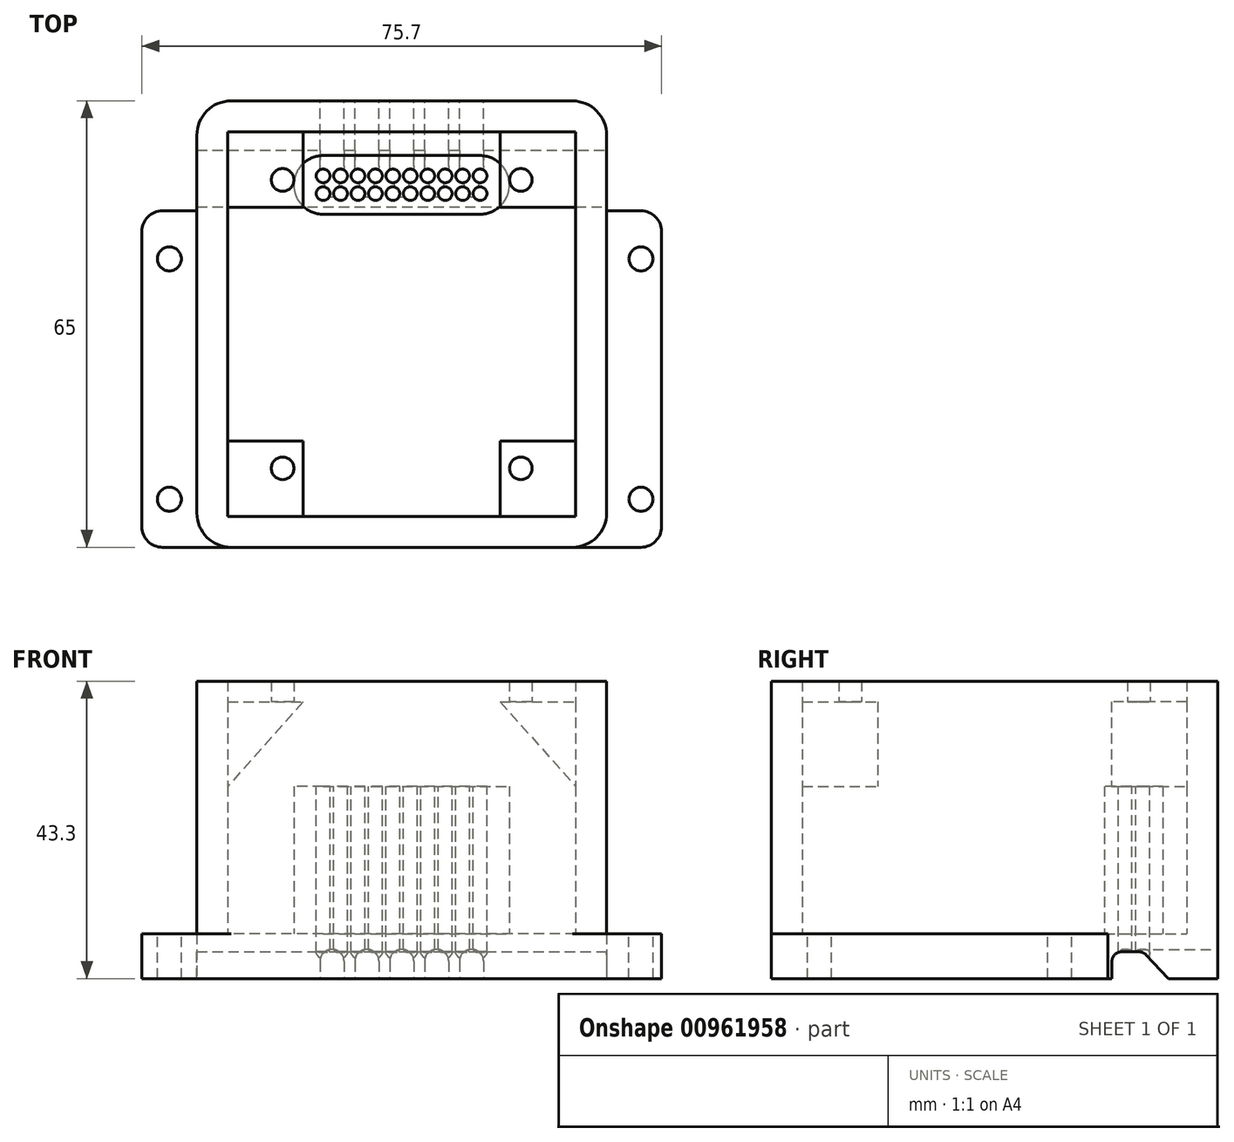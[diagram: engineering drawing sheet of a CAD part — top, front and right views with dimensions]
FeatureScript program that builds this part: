
annotation { "Feature Type Name" : "Feature", "Feature Type Description" : "" }
export const myFeature = defineFeature(function(context is Context, id is Id, definition is map)
    precondition{}
    {
        {
            var Q0;
            Q0=qCreatedBy(makeId("Top.planeOp"),FACE);
            var sketch = newSketch(context, id + "F0", { "sketchPlane" : qUnion([Q0])});
            skLineSegment(sketch, "E0.bottom", {"start": v(22.35, -25) * mm, "end": v(-22.35, -25) * mm});
            skLineSegment(sketch, "E0.top", {"start": v(22.35, 25) * mm, "end": v(-22.35, 25) * mm});
            skLineSegment(sketch, "E0.left", {"start": v(22.35, -25) * mm, "end": v(22.35, 25) * mm});
            skLineSegment(sketch, "E0.right", {"start": v(-22.35, -25) * mm, "end": v(-22.35, 25) * mm});
            skPoint(sketch, "E0.middle", {"position": v(0, 0) * mm});
            skSolve(sketch);
        }
        {
            var Q0;
            Q0=qCreatedBy(makeId("Top.planeOp"),FACE);
            var sketch = newSketch(context, id + "F1", { "sketchPlane" : qUnion([Q0])});
            skLineSegment(sketch, "E1.bottom", {"start": v(29.85, -32.5) * mm, "end": v(-29.85, -32.5) * mm});
            skLineSegment(sketch, "E1.top", {"start": v(24.85, 32.5) * mm, "end": v(-24.85, 32.5) * mm});
            skLineSegment(sketch, "E1.left", {"start": v(29.85, -32.5) * mm, "end": v(29.85, 27.5) * mm});
            skLineSegment(sketch, "E1.right", {"start": v(-29.85, -32.5) * mm, "end": v(-29.85, 27.5) * mm});
            skPoint(sketch, "E1.middle", {"position": v(0, 0) * mm});
            skPoint(sketch, "E2.visualSharp", {"position": v(-29.85, 32.5) * mm});
            skArc(sketch, "E2.filletArc", {"start": v(-24.85, 32.5) * mm, "mid": v(-28.39, 31.04) * mm, "end": v(-29.85, 27.5) * mm});
            skPoint(sketch, "E3.visualSharp", {"position": v(29.85, 32.5) * mm});
            skArc(sketch, "E3.filletArc", {"start": v(29.85, 27.5) * mm, "mid": v(28.39, 31.04) * mm, "end": v(24.85, 32.5) * mm});
            skPoint(sketch, "E4.visualSharp", {"position": v(-29.85, -32.5) * mm});
            skPoint(sketch, "E5.visualSharp", {"position": v(29.85, -32.5) * mm});
            skLineSegment(sketch, "E6", {"start": v(-20.98, 18.5) * mm, "end": v(20.45, 18.5) * mm, "construction": true});
            skLineSegment(sketch, "E7.bottom", {"start": v(-29.85, -32.5) * mm, "end": v(-34.85, -32.5) * mm});
            skLineSegment(sketch, "E7.top", {"start": v(-29.85, 16.5) * mm, "end": v(-34.85, 16.5) * mm});
            skLineSegment(sketch, "E7.left", {"start": v(-29.85, -32.5) * mm, "end": v(-29.85, 16.5) * mm});
            skLineSegment(sketch, "E7.right", {"start": v(-37.85, -29.5) * mm, "end": v(-37.85, 13.5) * mm});
            skPoint(sketch, "E8.oppositeSnap0", {"position": v(-33.85, 16.5) * mm});
            skLineSegment(sketch, "E8.bottom", {"start": v(29.85, -32.5) * mm, "end": v(34.85, -32.5) * mm});
            skLineSegment(sketch, "E8.top", {"start": v(29.85, 16.5) * mm, "end": v(34.85, 16.5) * mm});
            skLineSegment(sketch, "E8.left", {"start": v(29.85, -32.5) * mm, "end": v(29.85, 16.5) * mm});
            skLineSegment(sketch, "E8.right", {"start": v(37.85, -29.5) * mm, "end": v(37.85, 13.5) * mm});
            skPoint(sketch, "E9.visualSharp", {"position": v(-37.85, 16.5) * mm});
            skArc(sketch, "E9.filletArc", {"start": v(-34.85, 16.5) * mm, "mid": v(-36.97, 15.62) * mm, "end": v(-37.85, 13.5) * mm});
            skPoint(sketch, "E10.visualSharp", {"position": v(-37.85, -32.5) * mm});
            skArc(sketch, "E10.filletArc", {"start": v(-37.85, -29.5) * mm, "mid": v(-36.97, -31.62) * mm, "end": v(-34.85, -32.5) * mm});
            skPoint(sketch, "E11.visualSharp", {"position": v(37.85, 16.5) * mm});
            skArc(sketch, "E11.filletArc", {"start": v(37.85, 13.5) * mm, "mid": v(36.97, 15.62) * mm, "end": v(34.85, 16.5) * mm});
            skPoint(sketch, "E12.visualSharp", {"position": v(37.85, -32.5) * mm});
            skArc(sketch, "E12.filletArc", {"start": v(34.85, -32.5) * mm, "mid": v(36.97, -31.62) * mm, "end": v(37.85, -29.5) * mm});
            skSolve(sketch);
        }
        {
            var Q0;
            Q0=makeQuery(id+"F1.imprint","IMPRINT",FACE,{"disambiguationData":[TD([[makeQuery(id+"F1.imprint","IMPRINT",EDGE,{"derivedFrom":sQuery(id+"F1.wireOp",EDGE,"E1.bottom")}),-1.0]])]});
            var Q1;
            Q1=makeQuery(id+"F1.imprint","IMPRINT",FACE,{"disambiguationData":[TD([[makeQuery(id+"F1.imprint","IMPRINT",EDGE,{"derivedFrom":sQuery(id+"F1.wireOp",EDGE,"E7.bottom")}),-1.0]])]});
            var Q2;
            Q2=makeQuery(id+"F1.imprint","IMPRINT",FACE,{"disambiguationData":[TD([[makeQuery(id+"F1.imprint","IMPRINT",EDGE,{"derivedFrom":sQuery(id+"F1.wireOp",EDGE,"E8.bottom")}),1.0]])]});
            extrude(context, id + "F2", {"entities" : qUnion([Q0, Q1, Q2]), "depth" : 6.5 * mm, "offsetDistance" : 25 * mm});
        }
        {
            var Q0;
            Q0=makeQuery(id+"F2.opExtrude","CAP_FACE",FACE,{"disambiguationData":[OSD([sQuery(id+"F1.wireOp",EDGE,"E1.bottom"),sQuery(id+"F1.wireOp",EDGE,"E1.top"),sQuery(id+"F1.wireOp",EDGE,"E1.left"),sQuery(id+"F1.wireOp",EDGE,"E1.right"),sQuery(id+"F1.wireOp",EDGE,"E2.filletArc"),sQuery(id+"F1.wireOp",EDGE,"E3.filletArc"),sQuery(id+"F1.wireOp",EDGE,"E4.filletArc"),sQuery(id+"F1.wireOp",EDGE,"E5.filletArc")])],"isStart":false});
            var sketch = newSketch(context, id + "F3", { "sketchPlane" : qUnion([Q0])});
            skLineSegment(sketch, "E13.bottom", {"start": v(25.35, -28) * mm, "end": v(-25.35, -28) * mm});
            skLineSegment(sketch, "E13.top", {"start": v(25.35, 28) * mm, "end": v(-25.35, 28) * mm});
            skLineSegment(sketch, "E13.left", {"start": v(25.35, -28) * mm, "end": v(25.35, 28) * mm});
            skLineSegment(sketch, "E13.right", {"start": v(-25.35, -28) * mm, "end": v(-25.35, 28) * mm});
            skPoint(sketch, "E13.middle", {"position": v(0, 0) * mm});
            skLineSegment(sketch, "E14.bottom", {"start": v(-15.24, 28) * mm, "end": v(15.24, 28) * mm});
            skLineSegment(sketch, "E14.top", {"start": v(-11.45, 16) * mm, "end": v(11.4, 16) * mm});
            skPoint(sketch, "E15", {"position": v(-11.45, 19) * mm});
            skPoint(sketch, "E16", {"position": v(-8.91, 19) * mm});
            skPoint(sketch, "E17", {"position": v(-6.37, 19) * mm});
            skPoint(sketch, "E18", {"position": v(-3.83, 19) * mm});
            skPoint(sketch, "E19", {"position": v(-1.3, 19) * mm});
            skPoint(sketch, "E20", {"position": v(1.25, 19) * mm});
            skPoint(sketch, "E21", {"position": v(3.79, 19) * mm});
            skPoint(sketch, "E22", {"position": v(6.33, 19) * mm});
            skPoint(sketch, "E23", {"position": v(8.87, 19) * mm});
            skPoint(sketch, "E24", {"position": v(11.4, 19) * mm});
            skPoint(sketch, "E25.visualSharp", {"position": v(15.24, 16) * mm});
            skLineSegment(sketch, "E26.top", {"start": v(-11.45, 24.54) * mm, "end": v(11.4, 24.54) * mm});
            skArc(sketch, "E27", {"start": v(-11.45, 24.54) * mm, "mid": v(-15.72, 20.27) * mm, "end": v(-11.45, 16) * mm});
            skArc(sketch, "E28", {"start": v(11.4, 16) * mm, "mid": v(15.68, 20.27) * mm, "end": v(11.4, 24.54) * mm});
            skLineSegment(sketch, "E29.bottom", {"start": v(24.85, -32.5) * mm, "end": v(-24.85, -32.5) * mm});
            skLineSegment(sketch, "E29.top", {"start": v(24.85, 32.5) * mm, "end": v(-24.85, 32.5) * mm});
            skLineSegment(sketch, "E29.left", {"start": v(29.85, -27.5) * mm, "end": v(29.85, 27.5) * mm});
            skLineSegment(sketch, "E29.right", {"start": v(-29.85, -27.5) * mm, "end": v(-29.85, 27.5) * mm});
            skPoint(sketch, "E30.visualSharp", {"position": v(-29.85, -32.5) * mm});
            skArc(sketch, "E30.filletArc", {"start": v(-29.85, -27.5) * mm, "mid": v(-28.39, -31.04) * mm, "end": v(-24.85, -32.5) * mm});
            skPoint(sketch, "E31.visualSharp", {"position": v(29.85, -32.5) * mm});
            skArc(sketch, "E31.filletArc", {"start": v(24.85, -32.5) * mm, "mid": v(28.39, -31.04) * mm, "end": v(29.85, -27.5) * mm});
            skPoint(sketch, "E32.visualSharp", {"position": v(-29.85, 32.5) * mm});
            skArc(sketch, "E32.filletArc", {"start": v(-24.85, 32.5) * mm, "mid": v(-28.39, 31.04) * mm, "end": v(-29.85, 27.5) * mm});
            skPoint(sketch, "E33.visualSharp", {"position": v(29.85, 32.5) * mm});
            skArc(sketch, "E33.filletArc", {"start": v(29.85, 27.5) * mm, "mid": v(28.39, 31.04) * mm, "end": v(24.85, 32.5) * mm});
            skPoint(sketch, "E34", {"position": v(-6.37, 21.54) * mm});
            skPoint(sketch, "E35", {"position": v(-11.45, 21.54) * mm});
            skPoint(sketch, "E36", {"position": v(-8.91, 21.54) * mm});
            skPoint(sketch, "E37", {"position": v(-3.83, 21.54) * mm});
            skPoint(sketch, "E38", {"position": v(-1.3, 21.54) * mm});
            skPoint(sketch, "E39", {"position": v(1.25, 21.54) * mm});
            skPoint(sketch, "E40", {"position": v(3.79, 21.54) * mm});
            skPoint(sketch, "E41", {"position": v(6.33, 21.54) * mm});
            skPoint(sketch, "E42", {"position": v(8.87, 21.54) * mm});
            skPoint(sketch, "E43", {"position": v(11.4, 21.54) * mm});
            skSolve(sketch);
        }
        {
            var Q0;
            Q0=makeQuery(id+"F3.imprint","IMPRINT",FACE,{"disambiguationData":[TD([[makeQuery(id+"F3.imprint","IMPRINT",EDGE,{"derivedFrom":sQuery(id+"F3.wireOp",EDGE,"E13.bottom")}),1.0]])]});
            var Q1;
            Q1=makeQuery(id+"F3.imprint","IMPRINT",FACE,{"disambiguationData":[TD([[makeQuery(id+"F3.imprint","IMPRINT",EDGE,{"derivedFrom":sQuery(id+"F3.wireOp",EDGE,"E14.top")}),1.0]])]});
            extrude(context, id + "F4", {"entities" : qUnion([Q0, Q1]), "operationType" : NewBodyOperationType.ADD, "depth" : 21.5 * mm, "offsetDistance" : 25 * mm});
        }
        {
            var Q0;
            {var subQ0=sQuery(id+"F1.wireOp",EDGE,"E1.left");Q0=makeQuery(id+"F4.boolean.opBoolean","MERGE",FACE,{"derivedFrom":[makeQuery(id+"F2.opExtrude","SWEPT_FACE",FACE,{"disambiguationData":[OSD([subQ0])]}),makeQuery(id+"F4.opExtrude","SWEPT_FACE",FACE,{"disambiguationData":[OSD([subQ0])]})]});}
            var sketch = newSketch(context, id + "F5", { "sketchPlane" : qUnion([Q0])});
            skLineSegment(sketch, "E44", {"start": v(18.5, 18.6) * mm, "end": v(18.5, -3.34) * mm, "construction": true});
            skPoint(sketch, "E45", {"position": v(18.5, 2.5) * mm});
            skCircle(sketch, "E46", {"center": v(18.5, 2.5) * mm, "radius": 1.4 * mm});
            skLineSegment(sketch, "E47", {"start": v(17.1, 2.5) * mm, "end": v(17.1, 0) * mm});
            skCircle(sketch, "E48", {"center": v(21.04, 2.5) * mm, "radius": 1.4 * mm});
            skLineSegment(sketch, "E49", {"start": v(-11765.86, 3.9) * mm, "end": v(18.5, 3.9) * mm});
            skLineSegment(sketch, "E50", {"start": v(22.06, 3.46) * mm, "end": v(25.34, 0) * mm});
            skLineSegment(sketch, "E51", {"start": v(18.5, 3.9) * mm, "end": v(21.04, 3.9) * mm});
            skSolve(sketch);
        }
        {
            var Q0;
            {var subQ0=sQuery(id+"F5.wireOp",EDGE,"E46");var subQ1=makeQuery(id+"F5.imprint","INTERSECT",VERTEX,{"derivedFrom":[subQ0,sQuery(id+"F5.wireOp",EDGE,"E47")]});Q0=makeQuery(id+"F5.imprint","IMPRINT",FACE,{"disambiguationData":[TD([[makeQuery(id+"F5.imprint","IMPRINT",EDGE,{"disambiguationData":[TD([[subQ1,1.0]])],"derivedFrom":subQ0}),1.0]])]});}
            var Q1;
            {var subQ0=sQuery(id+"F5.wireOp",EDGE,"E47");Q1=makeQuery(id+"F5.imprint","IMPRINT",FACE,{"disambiguationData":[TD([[makeQuery(id+"F5.imprint","IMPRINT",EDGE,{"derivedFrom":subQ0}),1.0]])]});}
            var Q2;
            {var subQ0=sQuery(id+"F5.wireOp",EDGE,"E51");Q2=makeQuery(id+"F5.imprint","IMPRINT",FACE,{"disambiguationData":[TD([[makeQuery(id+"F5.imprint","IMPRINT",EDGE,{"derivedFrom":subQ0}),-1.0]])]});}
            var Q3;
            {var subQ0=sQuery(id+"F5.wireOp",EDGE,"E48");var subQ1=sQuery(id+"F5.wireOp",EDGE,"E46");var subQ2=makeQuery(id+"F5.imprint","INTERSECT",VERTEX,{"disambiguationData":[OD(0.0)],"derivedFrom":[subQ1,subQ0]});Q3=makeQuery(id+"F5.imprint","IMPRINT",FACE,{"disambiguationData":[TD([[makeQuery(id+"F5.imprint","IMPRINT",EDGE,{"disambiguationData":[TD([[subQ2,1.0]])],"derivedFrom":subQ1}),-1.0]])]});}
            var Q4;
            {var subQ0=sQuery(id+"F5.wireOp",EDGE,"E48");var subQ1=sQuery(id+"F5.wireOp",EDGE,"E46");var subQ2=makeQuery(id+"F5.imprint","INTERSECT",VERTEX,{"disambiguationData":[OD(0.0)],"derivedFrom":[subQ1,subQ0]});Q4=makeQuery(id+"F5.imprint","IMPRINT",FACE,{"disambiguationData":[TD([[makeQuery(id+"F5.imprint","IMPRINT",EDGE,{"disambiguationData":[TD([[subQ2,1.0]])],"derivedFrom":subQ1}),1.0]])]});}
            extrude(context, id + "F6", {"entities" : qUnion([Q0, Q1, Q2, Q3, Q4]), "operationType" : NewBodyOperationType.REMOVE, "endBound" : BoundingType.THROUGH_ALL, "oppositeDirection" : true, "depth" : 25 * mm, "offsetDistance" : 25 * mm});
        }
        {
            var Q0;
            Q0=makeQuery(id+"F4.opExtrude","CAP_FACE",FACE,{"disambiguationData":[OSD([sQuery(id+"F3.wireOp",EDGE,"E13.bottom"),sQuery(id+"F3.wireOp",EDGE,"E13.top"),sQuery(id+"F3.wireOp",EDGE,"E13.left"),sQuery(id+"F3.wireOp",EDGE,"E13.right"),sQuery(id+"F3.wireOp",EDGE,"E29.bottom"),sQuery(id+"F3.wireOp",EDGE,"E29.top"),sQuery(id+"F3.wireOp",EDGE,"E29.left"),sQuery(id+"F3.wireOp",EDGE,"E29.right"),sQuery(id+"F3.wireOp",EDGE,"E30.filletArc"),sQuery(id+"F3.wireOp",EDGE,"E31.filletArc"),sQuery(id+"F3.wireOp",EDGE,"E32.filletArc"),sQuery(id+"F3.wireOp",EDGE,"E33.filletArc")])],"isStart":false});
            var sketch = newSketch(context, id + "F7", { "sketchPlane" : qUnion([Q0])});
            skPoint(sketch, "E52", {"position": v(-11.45, 19) * mm});
            skCircle(sketch, "E53", {"center": v(-11.45, 19) * mm, "radius": 1 * mm});
            skPoint(sketch, "E54", {"position": v(-8.91, 19) * mm});
            skPoint(sketch, "E55", {"position": v(-6.37, 19) * mm});
            skPoint(sketch, "E56", {"position": v(-3.83, 19) * mm});
            skPoint(sketch, "E57", {"position": v(-1.3, 19) * mm});
            skPoint(sketch, "E58", {"position": v(1.25, 19) * mm});
            skPoint(sketch, "E59", {"position": v(3.79, 19) * mm});
            skPoint(sketch, "E60", {"position": v(6.33, 19) * mm});
            skPoint(sketch, "E61", {"position": v(8.87, 19) * mm});
            skPoint(sketch, "E62", {"position": v(11.4, 19) * mm});
            skCircle(sketch, "E63", {"center": v(-8.91, 19) * mm, "radius": 1 * mm});
            skCircle(sketch, "E64", {"center": v(-6.37, 19) * mm, "radius": 1 * mm});
            skCircle(sketch, "E65", {"center": v(-3.83, 19) * mm, "radius": 1 * mm});
            skCircle(sketch, "E66", {"center": v(-1.3, 19) * mm, "radius": 1 * mm});
            skCircle(sketch, "E67", {"center": v(1.25, 19) * mm, "radius": 1 * mm});
            skCircle(sketch, "E68", {"center": v(3.79, 19) * mm, "radius": 1 * mm});
            skCircle(sketch, "E69", {"center": v(6.33, 19) * mm, "radius": 1 * mm});
            skCircle(sketch, "E70", {"center": v(8.87, 19) * mm, "radius": 1 * mm});
            skCircle(sketch, "E71", {"center": v(11.4, 19) * mm, "radius": 1 * mm});
            skPoint(sketch, "E72", {"position": v(-11.45, 21.58) * mm});
            skPoint(sketch, "E73", {"position": v(-8.91, 21.58) * mm});
            skPoint(sketch, "E74", {"position": v(-6.37, 21.58) * mm});
            skPoint(sketch, "E75", {"position": v(-3.83, 21.58) * mm});
            skPoint(sketch, "E76", {"position": v(-1.3, 21.58) * mm});
            skPoint(sketch, "E77", {"position": v(1.25, 21.58) * mm});
            skPoint(sketch, "E78", {"position": v(3.79, 21.58) * mm});
            skPoint(sketch, "E79", {"position": v(6.33, 21.58) * mm});
            skPoint(sketch, "E80", {"position": v(8.87, 21.58) * mm});
            skPoint(sketch, "E81", {"position": v(11.4, 21.58) * mm});
            skCircle(sketch, "E82", {"center": v(-11.45, 21.58) * mm, "radius": 1 * mm});
            skCircle(sketch, "E83", {"center": v(-8.91, 21.58) * mm, "radius": 1 * mm});
            skCircle(sketch, "E84", {"center": v(-6.37, 21.58) * mm, "radius": 1 * mm});
            skCircle(sketch, "E85", {"center": v(-3.83, 21.58) * mm, "radius": 1 * mm});
            skCircle(sketch, "E86", {"center": v(-4.8, 18.76) * mm, "radius": 0.8 * mm});
            skCircle(sketch, "E87", {"center": v(-1.3, 21.58) * mm, "radius": 1 * mm});
            skCircle(sketch, "E88", {"center": v(1.25, 21.58) * mm, "radius": 1 * mm});
            skCircle(sketch, "E89", {"center": v(3.79, 21.58) * mm, "radius": 1 * mm});
            skCircle(sketch, "E90", {"center": v(6.33, 21.58) * mm, "radius": 1 * mm});
            skCircle(sketch, "E91", {"center": v(8.87, 21.58) * mm, "radius": 1 * mm});
            skCircle(sketch, "E92", {"center": v(11.4, 21.58) * mm, "radius": 1 * mm});
            skSolve(sketch);
        }
        {
            var Q0;
            {var subQ0=sQuery(id+"F1.wireOp",EDGE,"E1.left");Q0=makeQuery(id+"F4.boolean.opBoolean","MERGE",FACE,{"derivedFrom":[makeQuery(id+"F2.opExtrude","SWEPT_FACE",FACE,{"disambiguationData":[OSD([subQ0])]}),makeQuery(id+"F4.opExtrude","SWEPT_FACE",FACE,{"disambiguationData":[OSD([subQ0])]})]});}
            var sketch = newSketch(context, id + "F8", { "sketchPlane" : qUnion([Q0])});
            skSolve(sketch);
        }
        {
            var Q0;
            Q0=makeQuery(id+"F7.imprint","IMPRINT",FACE,{"disambiguationData":[TD([[makeQuery(id+"F7.imprint","IMPRINT",EDGE,{"derivedFrom":sQuery(id+"F7.wireOp",EDGE,"E66")}),1.0]])]});
            var Q1;
            Q1=makeQuery(id+"F7.imprint","IMPRINT",FACE,{"disambiguationData":[TD([[makeQuery(id+"F7.imprint","IMPRINT",EDGE,{"derivedFrom":sQuery(id+"F7.wireOp",EDGE,"E53")}),1.0]])]});
            var Q2;
            Q2=makeQuery(id+"F7.imprint","IMPRINT",FACE,{"disambiguationData":[TD([[makeQuery(id+"F7.imprint","IMPRINT",EDGE,{"derivedFrom":sQuery(id+"F7.wireOp",EDGE,"E63")}),1.0]])]});
            var Q3;
            Q3=makeQuery(id+"F7.imprint","IMPRINT",FACE,{"disambiguationData":[TD([[makeQuery(id+"F7.imprint","IMPRINT",EDGE,{"derivedFrom":sQuery(id+"F7.wireOp",EDGE,"E64")}),1.0]])]});
            var Q4;
            Q4=makeQuery(id+"F7.imprint","IMPRINT",FACE,{"disambiguationData":[TD([[makeQuery(id+"F7.imprint","IMPRINT",EDGE,{"derivedFrom":sQuery(id+"F7.wireOp",EDGE,"E65")}),1.0]])]});
            var Q5;
            Q5=makeQuery(id+"F7.imprint","IMPRINT",FACE,{"disambiguationData":[TD([[makeQuery(id+"F7.imprint","IMPRINT",EDGE,{"derivedFrom":sQuery(id+"F7.wireOp",EDGE,"E67")}),1.0]])]});
            var Q6;
            Q6=makeQuery(id+"F7.imprint","IMPRINT",FACE,{"disambiguationData":[TD([[makeQuery(id+"F7.imprint","IMPRINT",EDGE,{"derivedFrom":sQuery(id+"F7.wireOp",EDGE,"E68")}),1.0]])]});
            var Q7;
            Q7=makeQuery(id+"F7.imprint","IMPRINT",FACE,{"disambiguationData":[TD([[makeQuery(id+"F7.imprint","IMPRINT",EDGE,{"derivedFrom":sQuery(id+"F7.wireOp",EDGE,"E69")}),1.0]])]});
            var Q8;
            Q8=makeQuery(id+"F7.imprint","IMPRINT",FACE,{"disambiguationData":[TD([[makeQuery(id+"F7.imprint","IMPRINT",EDGE,{"derivedFrom":sQuery(id+"F7.wireOp",EDGE,"E70")}),1.0]])]});
            var Q9;
            Q9=makeQuery(id+"F7.imprint","IMPRINT",FACE,{"disambiguationData":[TD([[makeQuery(id+"F7.imprint","IMPRINT",EDGE,{"derivedFrom":sQuery(id+"F7.wireOp",EDGE,"E71")}),1.0]])]});
            var Q10;
            Q10=makeQuery(id+"F7.imprint","IMPRINT",FACE,{"disambiguationData":[TD([[makeQuery(id+"F7.imprint","IMPRINT",EDGE,{"derivedFrom":sQuery(id+"F7.wireOp",EDGE,"E82")}),1.0]])]});
            var Q11;
            Q11=makeQuery(id+"F7.imprint","IMPRINT",FACE,{"disambiguationData":[TD([[makeQuery(id+"F7.imprint","IMPRINT",EDGE,{"derivedFrom":sQuery(id+"F7.wireOp",EDGE,"E83")}),1.0]])]});
            var Q12;
            Q12=makeQuery(id+"F7.imprint","IMPRINT",FACE,{"disambiguationData":[TD([[makeQuery(id+"F7.imprint","IMPRINT",EDGE,{"derivedFrom":sQuery(id+"F7.wireOp",EDGE,"E84")}),1.0]])]});
            var Q13;
            Q13=makeQuery(id+"F7.imprint","IMPRINT",FACE,{"disambiguationData":[TD([[makeQuery(id+"F7.imprint","IMPRINT",EDGE,{"derivedFrom":sQuery(id+"F7.wireOp",EDGE,"E85")}),1.0]])]});
            var Q14;
            Q14=makeQuery(id+"F7.imprint","IMPRINT",FACE,{"disambiguationData":[TD([[makeQuery(id+"F7.imprint","IMPRINT",EDGE,{"derivedFrom":sQuery(id+"F7.wireOp",EDGE,"E87")}),1.0]])]});
            var Q15;
            Q15=makeQuery(id+"F7.imprint","IMPRINT",FACE,{"disambiguationData":[TD([[makeQuery(id+"F7.imprint","IMPRINT",EDGE,{"derivedFrom":sQuery(id+"F7.wireOp",EDGE,"E88")}),1.0]])]});
            var Q16;
            Q16=makeQuery(id+"F7.imprint","IMPRINT",FACE,{"disambiguationData":[TD([[makeQuery(id+"F7.imprint","IMPRINT",EDGE,{"derivedFrom":sQuery(id+"F7.wireOp",EDGE,"E89")}),1.0]])]});
            var Q17;
            Q17=makeQuery(id+"F7.imprint","IMPRINT",FACE,{"disambiguationData":[TD([[makeQuery(id+"F7.imprint","IMPRINT",EDGE,{"derivedFrom":sQuery(id+"F7.wireOp",EDGE,"E90")}),1.0]])]});
            var Q18;
            Q18=makeQuery(id+"F7.imprint","IMPRINT",FACE,{"disambiguationData":[TD([[makeQuery(id+"F7.imprint","IMPRINT",EDGE,{"derivedFrom":sQuery(id+"F7.wireOp",EDGE,"E91")}),1.0]])]});
            var Q19;
            Q19=makeQuery(id+"F7.imprint","IMPRINT",FACE,{"disambiguationData":[TD([[makeQuery(id+"F7.imprint","IMPRINT",EDGE,{"derivedFrom":sQuery(id+"F7.wireOp",EDGE,"E92")}),1.0]])]});
            var Q20;
            Q20=qSketchRegion(id+"F8",true);
            extrude(context, id + "F9", {"entities" : qUnion([Q0, Q1, Q2, Q3, Q4, Q5, Q6, Q7, Q8, Q9, Q10, Q11, Q12, Q13, Q14, Q15, Q16, Q17, Q18, Q19, Q20]), "operationType" : NewBodyOperationType.REMOVE, "oppositeDirection" : true, "depth" : 26 * mm, "offsetDistance" : 25 * mm});
        }
        {
            var Q0;
            Q0=makeQuery(id+"F4.opExtrude","CAP_FACE",FACE,{"disambiguationData":[OSD([sQuery(id+"F3.wireOp",EDGE,"E13.bottom"),sQuery(id+"F3.wireOp",EDGE,"E13.top"),sQuery(id+"F3.wireOp",EDGE,"E13.left"),sQuery(id+"F3.wireOp",EDGE,"E13.right"),sQuery(id+"F3.wireOp",EDGE,"E29.bottom"),sQuery(id+"F3.wireOp",EDGE,"E29.top"),sQuery(id+"F3.wireOp",EDGE,"E29.left"),sQuery(id+"F3.wireOp",EDGE,"E29.right"),sQuery(id+"F3.wireOp",EDGE,"E30.filletArc"),sQuery(id+"F3.wireOp",EDGE,"E31.filletArc"),sQuery(id+"F3.wireOp",EDGE,"E32.filletArc"),sQuery(id+"F3.wireOp",EDGE,"E33.filletArc")])],"isStart":false});
            var sketch = newSketch(context, id + "F10", { "sketchPlane" : qUnion([Q0])});
            skLineSegment(sketch, "E93.bottom", {"start": v(-25.35, 28) * mm, "end": v(-14.35, 28) * mm});
            skLineSegment(sketch, "E93.top", {"start": v(-25.35, 17) * mm, "end": v(-14.35, 17) * mm});
            skLineSegment(sketch, "E93.left", {"start": v(-25.35, 28) * mm, "end": v(-25.35, 17) * mm});
            skLineSegment(sketch, "E93.right", {"start": v(-14.35, 28) * mm, "end": v(-14.35, 17) * mm});
            skLineSegment(sketch, "E94.bottom", {"start": v(25.35, 28) * mm, "end": v(14.35, 28) * mm});
            skLineSegment(sketch, "E94.top", {"start": v(25.35, 17) * mm, "end": v(14.35, 17) * mm});
            skLineSegment(sketch, "E94.left", {"start": v(25.35, 28) * mm, "end": v(25.35, 17) * mm});
            skLineSegment(sketch, "E94.right", {"start": v(14.35, 28) * mm, "end": v(14.35, 17) * mm});
            skLineSegment(sketch, "E95.bottom", {"start": v(-25.35, -28) * mm, "end": v(-14.35, -28) * mm});
            skLineSegment(sketch, "E95.top", {"start": v(-25.35, -17) * mm, "end": v(-14.35, -17) * mm});
            skLineSegment(sketch, "E95.left", {"start": v(-25.35, -28) * mm, "end": v(-25.35, -17) * mm});
            skLineSegment(sketch, "E95.right", {"start": v(-14.35, -28) * mm, "end": v(-14.35, -17) * mm});
            skLineSegment(sketch, "E96.bottom", {"start": v(25.35, -28) * mm, "end": v(14.35, -28) * mm});
            skLineSegment(sketch, "E96.top", {"start": v(25.35, -17) * mm, "end": v(14.35, -17) * mm});
            skLineSegment(sketch, "E96.left", {"start": v(25.35, -28) * mm, "end": v(25.35, -17) * mm});
            skLineSegment(sketch, "E96.right", {"start": v(14.35, -28) * mm, "end": v(14.35, -17) * mm});
            skSolve(sketch);
        }
        {
            var Q0;
            {var subQ5=sQuery(id+"F10.wireOp",EDGE,"E93.bottom");Q0=makeQuery(id+"F10.imprint","IMPRINT",FACE,{"disambiguationData":[TD([[makeQuery(id+"F10.imprint","IMPRINT",EDGE,{"derivedFrom":subQ5}),-1.0]])]});}
            var Q1;
            Q1=makeQuery(id+"F10.imprint","IMPRINT",FACE,{"disambiguationData":[TD([[makeQuery(id+"F10.imprint","IMPRINT",EDGE,{"derivedFrom":sQuery(id+"F10.wireOp",EDGE,"E93.bottom")}),1.0]])]});
            var Q2;
            Q2=makeQuery(id+"F10.imprint","IMPRINT",FACE,{"disambiguationData":[TD([[makeQuery(id+"F10.imprint","IMPRINT",EDGE,{"derivedFrom":sQuery(id+"F10.wireOp",EDGE,"E94.bottom")}),1.0]])]});
            var Q3;
            Q3=makeQuery(id+"F10.imprint","IMPRINT",FACE,{"disambiguationData":[TD([[makeQuery(id+"F10.imprint","IMPRINT",EDGE,{"derivedFrom":sQuery(id+"F10.wireOp",EDGE,"E95.bottom")}),-1.0]])]});
            var Q4;
            Q4=makeQuery(id+"F10.imprint","IMPRINT",FACE,{"disambiguationData":[TD([[makeQuery(id+"F10.imprint","IMPRINT",EDGE,{"derivedFrom":sQuery(id+"F10.wireOp",EDGE,"E96.bottom")}),-1.0]])]});
            extrude(context, id + "F11", {"entities" : qUnion([Q0, Q1, Q2, Q3, Q4]), "operationType" : NewBodyOperationType.ADD, "depth" : 12.3 * mm, "offsetDistance" : 25 * mm});
        }
        {
            var Q0;
            Q0=makeQuery(id+"F11.opExtrude","SWEPT_FACE",FACE,{"disambiguationData":[OSD([sQuery(id+"F10.wireOp",EDGE,"E93.top")])]});
            var sketch = newSketch(context, id + "F12", { "sketchPlane" : qUnion([Q0])});
            skLineSegment(sketch, "E97", {"start": v(-14.35, 40.3) * mm, "end": v(-25.35, 28) * mm});
            skLineSegment(sketch, "E98", {"start": v(-25.35, 28) * mm, "end": v(-14.35, 28) * mm});
            skLineSegment(sketch, "E99", {"start": v(-14.35, 28) * mm, "end": v(-14.35, 40.3) * mm});
            skSolve(sketch);
        }
        {
            var Q0;
            {var subQ0=sQuery(id+"F12.wireOp",EDGE,"E97");Q0=makeQuery(id+"F12.imprint","IMPRINT",FACE,{"disambiguationData":[TD([[makeQuery(id+"F12.imprint","IMPRINT",EDGE,{"derivedFrom":subQ0}),1.0]])]});}
            extrude(context, id + "F13", {"entities" : qUnion([Q0]), "operationType" : NewBodyOperationType.REMOVE, "oppositeDirection" : true, "depth" : 11 * mm, "offsetDistance" : 25 * mm});
        }
        {
            var Q0;
            Q0=makeQuery(id+"F11.opExtrude","SWEPT_FACE",FACE,{"disambiguationData":[OSD([sQuery(id+"F10.wireOp",EDGE,"E94.top")])]});
            var sketch = newSketch(context, id + "F14", { "sketchPlane" : qUnion([Q0])});
            skLineSegment(sketch, "E100", {"start": v(14.35, 40.3) * mm, "end": v(25.35, 28) * mm});
            skLineSegment(sketch, "E101", {"start": v(25.35, 28) * mm, "end": v(14.35, 28) * mm});
            skLineSegment(sketch, "E102", {"start": v(14.35, 28) * mm, "end": v(14.35, 40.3) * mm});
            skSolve(sketch);
        }
        {
            var Q0;
            {var subQ0=sQuery(id+"F14.wireOp",EDGE,"E100");Q0=makeQuery(id+"F14.imprint","IMPRINT",FACE,{"disambiguationData":[TD([[makeQuery(id+"F14.imprint","IMPRINT",EDGE,{"derivedFrom":subQ0}),-1.0]])]});}
            extrude(context, id + "F15", {"entities" : qUnion([Q0]), "operationType" : NewBodyOperationType.REMOVE, "oppositeDirection" : true, "depth" : 11 * mm, "offsetDistance" : 25 * mm});
        }
        {
            var Q0;
            Q0=makeQuery(id+"F11.opExtrude","SWEPT_FACE",FACE,{"disambiguationData":[OSD([sQuery(id+"F10.wireOp",EDGE,"E96.top")])]});
            var sketch = newSketch(context, id + "F16", { "sketchPlane" : qUnion([Q0])});
            skLineSegment(sketch, "E103", {"start": v(-25.35, 28) * mm, "end": v(-14.35, 40.3) * mm});
            skLineSegment(sketch, "E104", {"start": v(-14.35, 40.3) * mm, "end": v(-14.35, 28) * mm});
            skLineSegment(sketch, "E105", {"start": v(-14.35, 28) * mm, "end": v(-25.35, 28) * mm});
            skSolve(sketch);
        }
        {
            var Q0;
            Q0=makeQuery(id+"F16.imprint","IMPRINT",FACE,{"disambiguationData":[TD([[makeQuery(id+"F16.imprint","IMPRINT",EDGE,{"derivedFrom":sQuery(id+"F16.wireOp",EDGE,"E103")}),-1.0]])]});
            extrude(context, id + "F17", {"entities" : qUnion([Q0]), "operationType" : NewBodyOperationType.REMOVE, "oppositeDirection" : true, "depth" : 11 * mm, "offsetDistance" : 25 * mm});
        }
        {
            var Q0;
            Q0=makeQuery(id+"F11.opExtrude","SWEPT_FACE",FACE,{"disambiguationData":[OSD([sQuery(id+"F10.wireOp",EDGE,"E95.top")])]});
            var sketch = newSketch(context, id + "F18", { "sketchPlane" : qUnion([Q0])});
            skLineSegment(sketch, "E106", {"start": v(14.35, 40.3) * mm, "end": v(25.35, 28) * mm});
            skLineSegment(sketch, "E107", {"start": v(25.35, 28) * mm, "end": v(14.35, 28) * mm});
            skLineSegment(sketch, "E108", {"start": v(14.35, 28) * mm, "end": v(14.35, 40.3) * mm});
            skSolve(sketch);
        }
        {
            var Q0;
            Q0=makeQuery(id+"F18.imprint","IMPRINT",FACE,{"disambiguationData":[TD([[makeQuery(id+"F18.imprint","IMPRINT",EDGE,{"derivedFrom":sQuery(id+"F18.wireOp",EDGE,"E106")}),-1.0]])]});
            extrude(context, id + "F19", {"entities" : qUnion([Q0]), "operationType" : NewBodyOperationType.REMOVE, "oppositeDirection" : true, "depth" : 11 * mm, "offsetDistance" : 25 * mm});
        }
        {
            var Q0;
            Q0=makeQuery(id+"F11.opExtrude","CAP_FACE",FACE,{"disambiguationData":[OSD([sQuery(id+"F3.wireOp",EDGE,"E13.bottom"),sQuery(id+"F3.wireOp",EDGE,"E13.top"),sQuery(id+"F3.wireOp",EDGE,"E13.left"),sQuery(id+"F3.wireOp",EDGE,"E13.right"),sQuery(id+"F3.wireOp",EDGE,"E29.bottom"),sQuery(id+"F3.wireOp",EDGE,"E29.top"),sQuery(id+"F3.wireOp",EDGE,"E29.left"),sQuery(id+"F3.wireOp",EDGE,"E29.right"),sQuery(id+"F3.wireOp",EDGE,"E30.filletArc"),sQuery(id+"F3.wireOp",EDGE,"E31.filletArc"),sQuery(id+"F3.wireOp",EDGE,"E32.filletArc"),sQuery(id+"F3.wireOp",EDGE,"E33.filletArc"),sQuery(id+"F10.wireOp",EDGE,"E93.top"),sQuery(id+"F10.wireOp",EDGE,"E93.right"),sQuery(id+"F10.wireOp",EDGE,"E94.top"),sQuery(id+"F10.wireOp",EDGE,"E94.right"),sQuery(id+"F10.wireOp",EDGE,"E95.top"),sQuery(id+"F10.wireOp",EDGE,"E95.right"),sQuery(id+"F10.wireOp",EDGE,"E96.top"),sQuery(id+"F10.wireOp",EDGE,"E96.right")])],"isStart":false});
            var sketch = newSketch(context, id + "F20", { "sketchPlane" : qUnion([Q0])});
            skPoint(sketch, "E109", {"position": v(-17.35, 21) * mm});
            skPoint(sketch, "E110", {"position": v(17.35, 21) * mm});
            skCircle(sketch, "E111", {"center": v(-17.35, 21) * mm, "radius": 1.65 * mm});
            skCircle(sketch, "E112", {"center": v(17.35, 21) * mm, "radius": 1.65 * mm});
            skLineSegment(sketch, "E113.bottom", {"start": v(-25.35, 28) * mm, "end": v(25.35, 28) * mm});
            skLineSegment(sketch, "E113.top", {"start": v(-25.35, -28) * mm, "end": v(25.35, -28) * mm});
            skLineSegment(sketch, "E113.left", {"start": v(-25.35, 28) * mm, "end": v(-25.35, -28) * mm});
            skLineSegment(sketch, "E113.right", {"start": v(25.35, 28) * mm, "end": v(25.35, -28) * mm});
            skPoint(sketch, "E114", {"position": v(-17.35, -21) * mm});
            skPoint(sketch, "E115", {"position": v(17.35, -21) * mm});
            skCircle(sketch, "E116", {"center": v(-17.35, -21) * mm, "radius": 1.65 * mm});
            skCircle(sketch, "E117", {"center": v(17.35, -21) * mm, "radius": 1.65 * mm});
            skSolve(sketch);
        }
        {
            var Q0;
            Q0=makeQuery(id+"F20.imprint","IMPRINT",FACE,{"disambiguationData":[TD([[makeQuery(id+"F20.imprint","IMPRINT",EDGE,{"derivedFrom":makeQuery(id+"F11.opExtrude","CAP_EDGE",EDGE,{"disambiguationData":[OSD([sQuery(id+"F1.wireOp",EDGE,"E1.bottom")])],"isStart":false})}),-1.0]])]});
            var Q1;
            Q1=makeQuery(id+"F20.imprint","IMPRINT",FACE,{"disambiguationData":[TD([[makeQuery(id+"F20.imprint","IMPRINT",EDGE,{"derivedFrom":sQuery(id+"F20.wireOp",EDGE,"E111")}),1.0]])]});
            var Q2;
            Q2=makeQuery(id+"F20.imprint","IMPRINT",FACE,{"disambiguationData":[TD([[makeQuery(id+"F20.imprint","IMPRINT",EDGE,{"derivedFrom":sQuery(id+"F20.wireOp",EDGE,"E112")}),1.0]])]});
            var Q3;
            Q3=makeQuery(id+"F20.imprint","IMPRINT",FACE,{"disambiguationData":[TD([[makeQuery(id+"F20.imprint","IMPRINT",EDGE,{"derivedFrom":sQuery(id+"F20.wireOp",EDGE,"E116")}),1.0]])]});
            var Q4;
            Q4=makeQuery(id+"F20.imprint","IMPRINT",FACE,{"disambiguationData":[TD([[makeQuery(id+"F20.imprint","IMPRINT",EDGE,{"derivedFrom":sQuery(id+"F20.wireOp",EDGE,"E117")}),1.0]])]});
            var Q5;
            Q5=makeQuery(id+"F20.imprint","IMPRINT",FACE,{"disambiguationData":[TD([[makeQuery(id+"F20.imprint","IMPRINT",EDGE,{"derivedFrom":makeQuery(id+"F11.opExtrude","CAP_EDGE",EDGE,{"disambiguationData":[OSD([sQuery(id+"F3.wireOp",EDGE,"E29.bottom")])],"isStart":false})}),-1.0]])]});
            extrude(context, id + "F21", {"entities" : qUnion([Q0, Q1, Q2, Q3, Q4, Q5]), "operationType" : NewBodyOperationType.ADD, "depth" : 3 * mm, "offsetDistance" : 25 * mm});
        }
        {
            var Q0;
            {var subQ0=sQuery(id+"F1.wireOp",EDGE,"E7.right");var subQ1=sQuery(id+"F1.wireOp",EDGE,"E7.top");var subQ2=sQuery(id+"F1.wireOp",EDGE,"E1.right");var subQ3=sQuery(id+"F1.wireOp",EDGE,"E8.bottom");var subQ4=sQuery(id+"F1.wireOp",EDGE,"E7.bottom");var subQ5=sQuery(id+"F1.wireOp",EDGE,"E1.bottom");var subQ6=sQuery(id+"F1.wireOp",EDGE,"E10.filletArc");var subQ7=sQuery(id+"F1.wireOp",EDGE,"E9.filletArc");Q0=makeQuery(id+"F4.boolean.opBoolean","SPLIT",FACE,{"disambiguationData":[TD([makeQuery(id+"F2.opExtrude","SWEPT_FACE",FACE,{"disambiguationData":[OSD([subQ2])]})])],"derivedFrom":makeQuery(id+"F2.opExtrude","CAP_FACE",FACE,{"disambiguationData":[OSD([subQ5,sQuery(id+"F1.wireOp",EDGE,"E1.top"),sQuery(id+"F1.wireOp",EDGE,"E1.left"),subQ2,sQuery(id+"F1.wireOp",EDGE,"E2.filletArc"),sQuery(id+"F1.wireOp",EDGE,"E3.filletArc"),subQ4,subQ1,subQ0,subQ3,sQuery(id+"F1.wireOp",EDGE,"E8.top"),sQuery(id+"F1.wireOp",EDGE,"E8.right"),subQ7,subQ6,sQuery(id+"F1.wireOp",EDGE,"E11.filletArc"),sQuery(id+"F1.wireOp",EDGE,"E12.filletArc")])],"isStart":false})});}
            var sketch = newSketch(context, id + "F22", { "sketchPlane" : qUnion([Q0])});
            skPoint(sketch, "E118", {"position": v(-33.85, 9.5) * mm});
            skPoint(sketch, "E119", {"position": v(34.85, 9.5) * mm});
            skPoint(sketch, "E120", {"position": v(34.85, -25.5) * mm});
            skPoint(sketch, "E121", {"position": v(-33.85, -25.5) * mm});
            skCircle(sketch, "E122", {"center": v(-33.85, 9.5) * mm, "radius": 1.75 * mm});
            skCircle(sketch, "E123", {"center": v(34.85, 9.5) * mm, "radius": 1.75 * mm});
            skCircle(sketch, "E124", {"center": v(-33.85, -25.5) * mm, "radius": 1.75 * mm});
            skCircle(sketch, "E125", {"center": v(34.85, -25.5) * mm, "radius": 1.75 * mm});
            skSolve(sketch);
        }
        {
            var Q0;
            Q0=makeQuery(id+"F22.imprint","IMPRINT",FACE,{"disambiguationData":[TD([[makeQuery(id+"F22.imprint","IMPRINT",EDGE,{"derivedFrom":sQuery(id+"F22.wireOp",EDGE,"E122")}),1.0]])]});
            var Q1;
            Q1=makeQuery(id+"F22.imprint","IMPRINT",FACE,{"disambiguationData":[TD([[makeQuery(id+"F22.imprint","IMPRINT",EDGE,{"derivedFrom":sQuery(id+"F22.wireOp",EDGE,"E124")}),1.0]])]});
            var Q2;
            Q2=makeQuery(id+"F22.imprint","IMPRINT",FACE,{"disambiguationData":[TD([[makeQuery(id+"F22.imprint","IMPRINT",EDGE,{"derivedFrom":sQuery(id+"F22.wireOp",EDGE,"E123")}),1.0]])]});
            var Q3;
            Q3=makeQuery(id+"F22.imprint","IMPRINT",FACE,{"disambiguationData":[TD([[makeQuery(id+"F22.imprint","IMPRINT",EDGE,{"derivedFrom":sQuery(id+"F22.wireOp",EDGE,"E125")}),1.0]])]});
            extrude(context, id + "F23", {"entities" : qUnion([Q0, Q1, Q2, Q3]), "operationType" : NewBodyOperationType.REMOVE, "endBound" : BoundingType.THROUGH_ALL, "oppositeDirection" : true, "depth" : 25 * mm, "offsetDistance" : 25 * mm});
        }
        {
            var Q0;
            {var subQ0=sQuery(id+"F3.wireOp",EDGE,"E29.top");Q0=makeQuery(id+"F21.boolean.opBoolean","MERGE",FACE,{"derivedFrom":[makeQuery(id+"F11.boolean.opBoolean","MERGE",FACE,{"derivedFrom":[makeQuery(id+"F4.boolean.opBoolean","MERGE",FACE,{"derivedFrom":[makeQuery(id+"F2.opExtrude","SWEPT_FACE",FACE,{"disambiguationData":[OSD([sQuery(id+"F1.wireOp",EDGE,"E1.top")])]}),makeQuery(id+"F4.opExtrude","SWEPT_FACE",FACE,{"disambiguationData":[OSD([subQ0])]})]}),makeQuery(id+"F11.opExtrude","SWEPT_FACE",FACE,{"disambiguationData":[OSD([subQ0])]})]}),makeQuery(id+"F21.opExtrude","SWEPT_FACE",FACE,{"disambiguationData":[OSD([subQ0])]})]});}
            var sketch = newSketch(context, id + "F24", { "sketchPlane" : qUnion([Q0])});
            skLineSegment(sketch, "E126", {"start": v(0, 0.67) * mm, "end": v(0, 43.3) * mm, "construction": true});
            skPoint(sketch, "E127", {"position": v(0, 2.5) * mm});
            skPoint(sketch, "E128", {"position": v(5.08, 2.5) * mm});
            skPoint(sketch, "E129", {"position": v(10.16, 2.5) * mm});
            skPoint(sketch, "E130", {"position": v(-5.08, 2.5) * mm});
            skPoint(sketch, "E131", {"position": v(-10.16, 2.5) * mm});
            skCircle(sketch, "E132", {"center": v(-10.16, 2.5) * mm, "radius": 1.75 * mm});
            skCircle(sketch, "E133", {"center": v(-5.08, 2.5) * mm, "radius": 1.75 * mm});
            skCircle(sketch, "E134", {"center": v(0, 2.5) * mm, "radius": 1.75 * mm});
            skCircle(sketch, "E135", {"center": v(5.08, 2.5) * mm, "radius": 1.75 * mm});
            skCircle(sketch, "E136", {"center": v(10.16, 2.5) * mm, "radius": 1.75 * mm});
            skLineSegment(sketch, "E137", {"start": v(-11.9, 2.5) * mm, "end": v(-11.9, 0) * mm});
            skLineSegment(sketch, "E138", {"start": v(-8.4, 2.5) * mm, "end": v(-8.4, 0) * mm});
            skLineSegment(sketch, "E139", {"start": v(-6.83, 2.5) * mm, "end": v(-6.83, 0) * mm});
            skLineSegment(sketch, "E140", {"start": v(-3.33, 2.5) * mm, "end": v(-3.33, 0) * mm});
            skLineSegment(sketch, "E141", {"start": v(-1.75, 2.5) * mm, "end": v(-1.75, 0) * mm});
            skLineSegment(sketch, "E142", {"start": v(1.75, 2.5) * mm, "end": v(1.75, 0) * mm});
            skLineSegment(sketch, "E143", {"start": v(6.83, 2.5) * mm, "end": v(6.83, 0) * mm});
            skLineSegment(sketch, "E144", {"start": v(3.33, 2.5) * mm, "end": v(3.33, 0) * mm});
            skLineSegment(sketch, "E145", {"start": v(8.4, 2.5) * mm, "end": v(8.4, 0) * mm});
            skLineSegment(sketch, "E146", {"start": v(11.9, 2.5) * mm, "end": v(11.9, 0) * mm});
            skSolve(sketch);
        }
        {
            var Q0;
            {var subQ0=sQuery(id+"F24.wireOp",EDGE,"E132");var subQ1=makeQuery(id+"F24.imprint","INTERSECT",VERTEX,{"derivedFrom":[subQ0,sQuery(id+"F24.wireOp",EDGE,"E137")]});Q0=makeQuery(id+"F24.imprint","IMPRINT",FACE,{"disambiguationData":[TD([[makeQuery(id+"F24.imprint","IMPRINT",EDGE,{"disambiguationData":[TD([[subQ1,1.0]])],"derivedFrom":subQ0}),1.0]])]});}
            var Q1;
            {var subQ0=sQuery(id+"F24.wireOp",EDGE,"E137");Q1=makeQuery(id+"F24.imprint","IMPRINT",FACE,{"disambiguationData":[TD([[makeQuery(id+"F24.imprint","IMPRINT",EDGE,{"derivedFrom":subQ0}),1.0]])]});}
            var Q2;
            {var subQ0=sQuery(id+"F24.wireOp",EDGE,"E133");var subQ1=makeQuery(id+"F24.imprint","INTERSECT",VERTEX,{"derivedFrom":[subQ0,sQuery(id+"F24.wireOp",EDGE,"E139")]});Q2=makeQuery(id+"F24.imprint","IMPRINT",FACE,{"disambiguationData":[TD([[makeQuery(id+"F24.imprint","IMPRINT",EDGE,{"disambiguationData":[TD([[subQ1,1.0]])],"derivedFrom":subQ0}),1.0]])]});}
            var Q3;
            {var subQ0=sQuery(id+"F24.wireOp",EDGE,"E139");Q3=makeQuery(id+"F24.imprint","IMPRINT",FACE,{"disambiguationData":[TD([[makeQuery(id+"F24.imprint","IMPRINT",EDGE,{"derivedFrom":subQ0}),1.0]])]});}
            var Q4;
            {var subQ0=sQuery(id+"F24.wireOp",EDGE,"E134");var subQ1=makeQuery(id+"F24.imprint","INTERSECT",VERTEX,{"derivedFrom":[subQ0,sQuery(id+"F24.wireOp",EDGE,"E141")]});Q4=makeQuery(id+"F24.imprint","IMPRINT",FACE,{"disambiguationData":[TD([[makeQuery(id+"F24.imprint","IMPRINT",EDGE,{"disambiguationData":[TD([[subQ1,1.0]])],"derivedFrom":subQ0}),1.0]])]});}
            var Q5;
            {var subQ0=sQuery(id+"F24.wireOp",EDGE,"E141");Q5=makeQuery(id+"F24.imprint","IMPRINT",FACE,{"disambiguationData":[TD([[makeQuery(id+"F24.imprint","IMPRINT",EDGE,{"derivedFrom":subQ0}),1.0]])]});}
            var Q6;
            {var subQ0=sQuery(id+"F24.wireOp",EDGE,"E135");var subQ1=makeQuery(id+"F24.imprint","INTERSECT",VERTEX,{"derivedFrom":[subQ0,sQuery(id+"F24.wireOp",EDGE,"E143")]});Q6=makeQuery(id+"F24.imprint","IMPRINT",FACE,{"disambiguationData":[TD([[makeQuery(id+"F24.imprint","IMPRINT",EDGE,{"disambiguationData":[TD([[subQ1,-1.0]])],"derivedFrom":subQ0}),1.0]])]});}
            var Q7;
            {var subQ0=sQuery(id+"F24.wireOp",EDGE,"E143");Q7=makeQuery(id+"F24.imprint","IMPRINT",FACE,{"disambiguationData":[TD([[makeQuery(id+"F24.imprint","IMPRINT",EDGE,{"derivedFrom":subQ0}),-1.0]])]});}
            var Q8;
            {var subQ0=sQuery(id+"F24.wireOp",EDGE,"E136");var subQ1=makeQuery(id+"F24.imprint","INTERSECT",VERTEX,{"derivedFrom":[subQ0,sQuery(id+"F24.wireOp",EDGE,"E145")]});Q8=makeQuery(id+"F24.imprint","IMPRINT",FACE,{"disambiguationData":[TD([[makeQuery(id+"F24.imprint","IMPRINT",EDGE,{"disambiguationData":[TD([[subQ1,1.0]])],"derivedFrom":subQ0}),1.0]])]});}
            var Q9;
            {var subQ0=sQuery(id+"F24.wireOp",EDGE,"E145");Q9=makeQuery(id+"F24.imprint","IMPRINT",FACE,{"disambiguationData":[TD([[makeQuery(id+"F24.imprint","IMPRINT",EDGE,{"derivedFrom":subQ0}),1.0]])]});}
            extrude(context, id + "F25", {"entities" : qUnion([Q0, Q1, Q2, Q3, Q4, Q5, Q6, Q7, Q8, Q9]), "operationType" : NewBodyOperationType.REMOVE, "oppositeDirection" : true, "depth" : 14 * mm, "offsetDistance" : 25 * mm});
        }
    });
